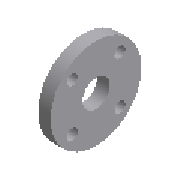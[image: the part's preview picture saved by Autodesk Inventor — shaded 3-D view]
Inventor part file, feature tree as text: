
AUTODESK INVENTOR PART (.ipt)
format: ipt  version: 2023.2 (Build 272271030, 271C)  size: 169,984 bytes
history: native  units: mm (DEFAULTED — no unit token found)
features: other x5, sketch x2, revolve x1, extrude x1, pattern_circular x1
ambient origin geometry x8: Origin, YZ Plane, XZ Plane, XY Plane, X Axis, Y Axis, Z Axis, Center Point
bodies: Solid1 (feature_tree)
feature tree (10):
  sketch  "Sketch1"  dims[d11=90.0deg d0=220.0mm]
  revolve  "Revolution1"  [1 undecoded]
  extrude  "Extrusion1"  Depth=22.0mm
  pattern_circular  "Circular Pattern1"  [2 undecoded]
  other  "Work Axis1"
  other  "Work Point1"
  other  "Work Point2"
  other  "Work Axis2"
  other  "Work Point3"
  sketch  "Sketch2"  dims[d1=22.0mm d2=180.0mm d19=25.4mm d3=0.0mm d4=80.0mm d5=360.0deg d6=116.0mm d7=18.0mm d8=22.5deg]
note: 3 required parameter values undecoded (feature->parameter linkage not recoverable at this tier; creation-order binding heuristic only, values carry confidence <= 0.55)